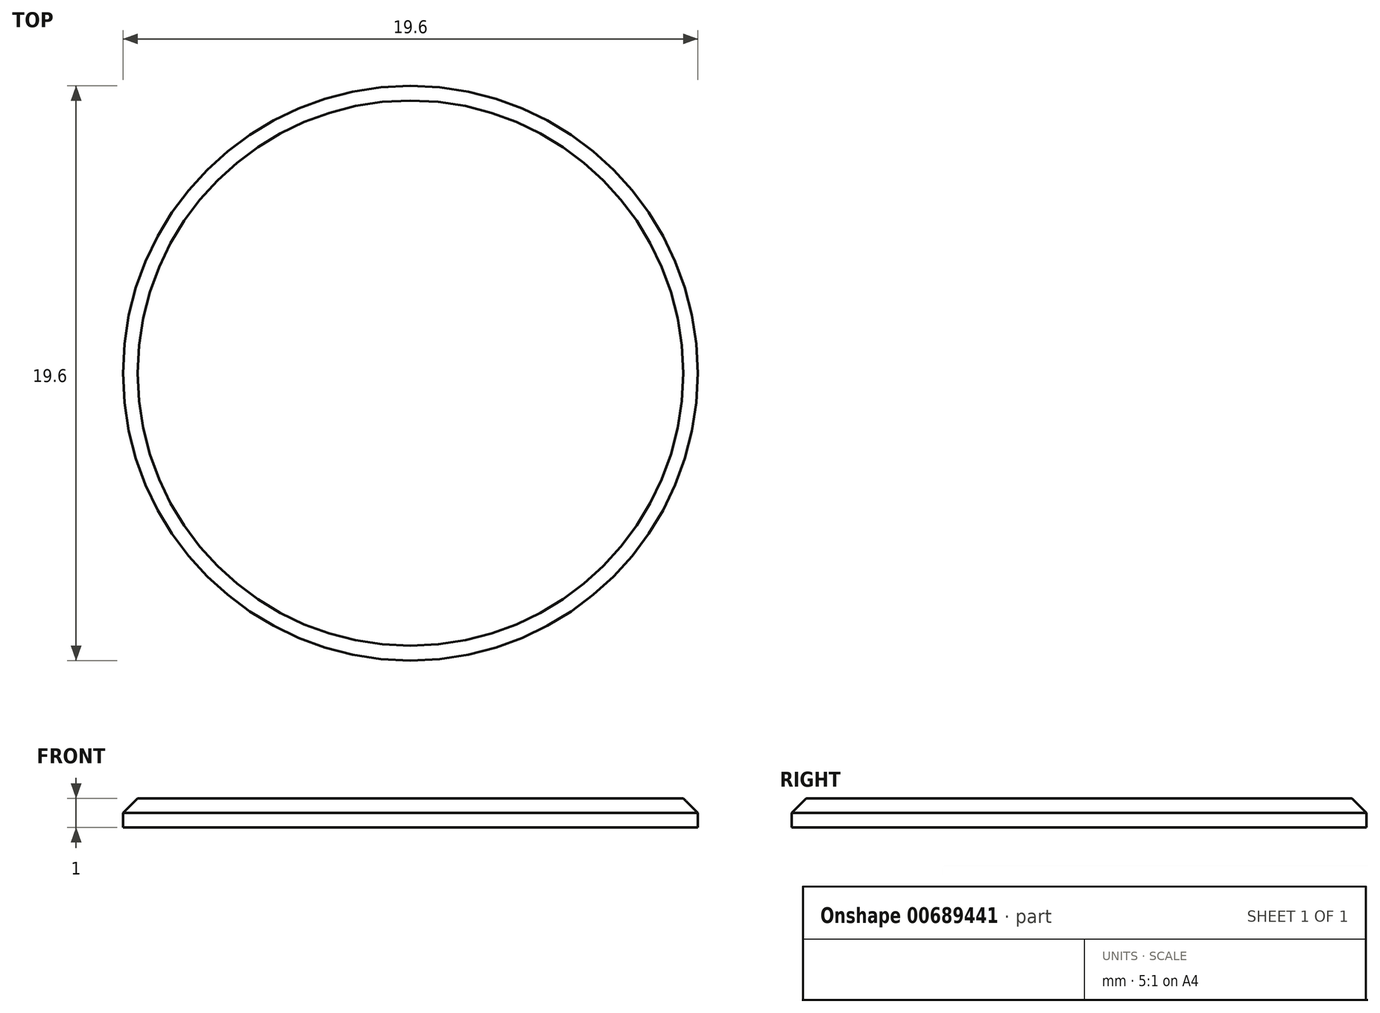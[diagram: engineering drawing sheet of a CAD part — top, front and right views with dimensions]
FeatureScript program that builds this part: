
annotation { "Feature Type Name" : "Feature", "Feature Type Description" : "" }
export const myFeature = defineFeature(function(context is Context, id is Id, definition is map)
    precondition{}
    {
        {
            var Q0;
            Q0=qCreatedBy(makeId("Top.planeOp"),FACE);
            var sketch = newSketch(context, id + "F0", { "sketchPlane" : qUnion([Q0])});
            skCircle(sketch, "E0", {"center": v(0, 0) * mm, "radius": 9.8 * mm});
            skSolve(sketch);
        }
        {
            var Q0;
            Q0=makeQuery(id+"F0.imprint","IMPRINT",FACE,{"disambiguationData":[TD([[makeQuery(id+"F0.imprint","IMPRINT",EDGE,{"derivedFrom":sQuery(id+"F0.wireOp",EDGE,"E0")}),1.0]])]});
            extrude(context, id + "F1", {"entities" : qUnion([Q0]), "depth" : 1 * mm, "offsetDistance" : 25 * mm});
        }
        {
            var Q0;
            Q0=makeQuery(id+"F1.opExtrude","CAP_EDGE",EDGE,{"disambiguationData":[OSD([sQuery(id+"F0.wireOp",EDGE,"E0")])],"isStart":false});
            chamfer(context, id + "F2", {"entities" : qUnion([Q0]), "width" : .5 * mm, "tangentPropagation" : true});
        }
    });
